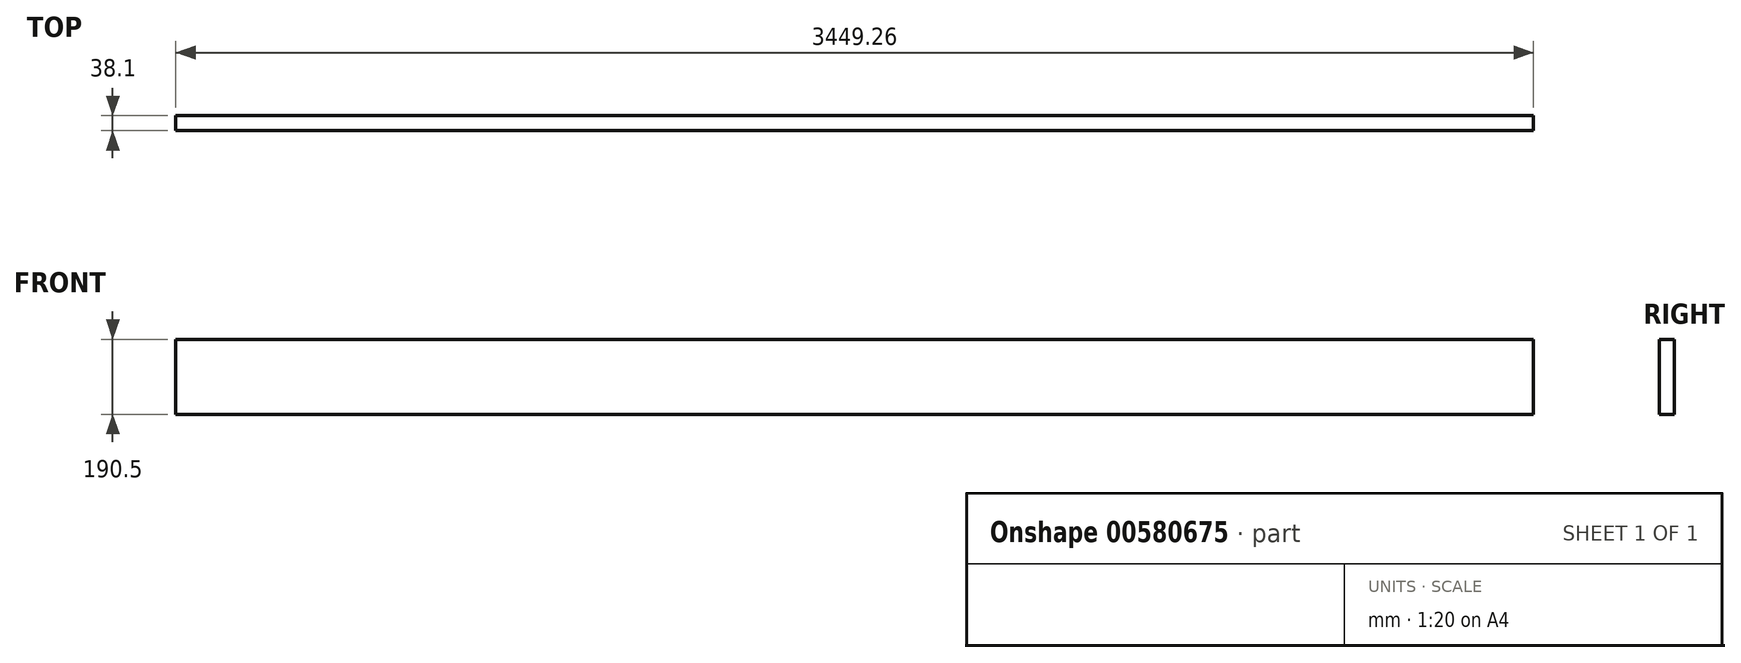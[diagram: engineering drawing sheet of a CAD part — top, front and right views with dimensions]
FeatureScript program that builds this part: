
annotation { "Feature Type Name" : "Feature", "Feature Type Description" : "" }
export const myFeature = defineFeature(function(context is Context, id is Id, definition is map)
    precondition{}
    {
        {
            var Q0;
            Q0=qCreatedBy(makeId("Top.planeOp"),FACE);
            var sketch = newSketch(context, id + "F0", { "sketchPlane" : qUnion([Q0])});
            skLineSegment(sketch, "E0.bottom", {"start": v(1724.63, -19.05) * mm, "end": v(-1724.63, -19.05) * mm});
            skLineSegment(sketch, "E0.top", {"start": v(1724.63, 19.05) * mm, "end": v(-1724.63, 19.05) * mm});
            skLineSegment(sketch, "E0.left", {"start": v(1724.63, -19.05) * mm, "end": v(1724.63, 19.05) * mm});
            skLineSegment(sketch, "E0.right", {"start": v(-1724.63, -19.05) * mm, "end": v(-1724.63, 19.05) * mm});
            skPoint(sketch, "E0.middle", {"position": v(0, 0) * mm});
            skSolve(sketch);
        }
        {
            var Q0;
            Q0=makeQuery(id+"F0.imprint","IMPRINT",FACE,{"disambiguationData":[TD([[makeQuery(id+"F0.imprint","IMPRINT",EDGE,{"derivedFrom":sQuery(id+"F0.wireOp",EDGE,"E0.bottom")}),-1.0]])]});
            extrude(context, id + "F1", {"entities" : qUnion([Q0]), "depth" : 190.5 * mm, "offsetDistance" : 25.4 * mm});
        }
    });
